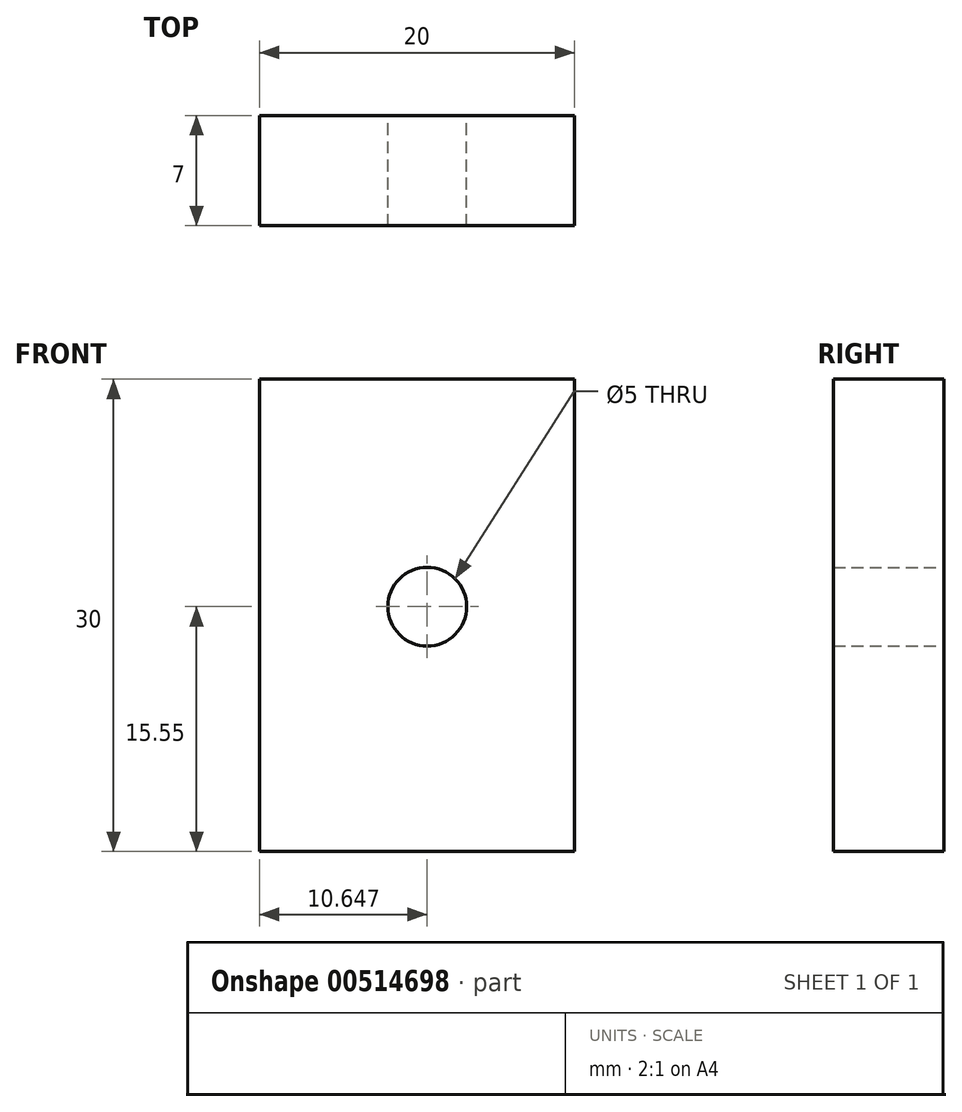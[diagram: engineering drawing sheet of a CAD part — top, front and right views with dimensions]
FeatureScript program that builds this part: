
annotation { "Feature Type Name" : "Feature", "Feature Type Description" : "" }
export const myFeature = defineFeature(function(context is Context, id is Id, definition is map)
    precondition{}
    {
        {
            var Q0;
            Q0=qCreatedBy(makeId("Top.planeOp"),FACE);
            var sketch = newSketch(context, id + "F0", { "sketchPlane" : qUnion([Q0])});
            skLineSegment(sketch, "E0", {"start": v(-34.41, 0) * mm, "end": v(35.74, 0) * mm, "construction": true});
            skLineSegment(sketch, "E1", {"start": v(0, 22.43) * mm, "end": v(0, -16.84) * mm, "construction": true});
            skLineSegment(sketch, "E2.bottom", {"start": v(0, 0) * mm, "end": v(20, 0) * mm});
            skLineSegment(sketch, "E2.top", {"start": v(0, 7) * mm, "end": v(20, 7) * mm});
            skLineSegment(sketch, "E2.left", {"start": v(0, 0) * mm, "end": v(0, 7) * mm});
            skLineSegment(sketch, "E2.right", {"start": v(20, 0) * mm, "end": v(20, 7) * mm});
            skSolve(sketch);
        }
        {
            var Q0;
            Q0=makeQuery(id+"F0.imprint","IMPRINT",FACE,{"disambiguationData":[TD([[makeQuery(id+"F0.imprint","IMPRINT",EDGE,{"derivedFrom":sQuery(id+"F0.wireOp",EDGE,"E2.bottom")}),1.0]])]});
            extrude(context, id + "F1", {"entities" : qUnion([Q0]), "depth" : 30 * mm, "offsetDistance" : 25 * mm});
        }
        {
            var Q0;
            Q0=makeQuery(id+"F1.opExtrude","SWEPT_FACE",FACE,{"disambiguationData":[OSD([sQuery(id+"F0.wireOp",EDGE,"E2.top")])]});
            var sketch = newSketch(context, id + "F2", { "sketchPlane" : qUnion([Q0])});
            skCircle(sketch, "E3", {"center": v(-10.65, 15.55) * mm, "radius": 2.5 * mm});
            skSolve(sketch);
        }
        {
            var Q0;
            Q0 = qSketchRegion(id + "F2", true);
            extrude(context, id + "F3", {"entities" : qUnion([Q0]), "operationType" : NewBodyOperationType.REMOVE, "oppositeDirection" : true, "depth" : 25 * mm, "offsetDistance" : 25 * mm});
        }
    });
